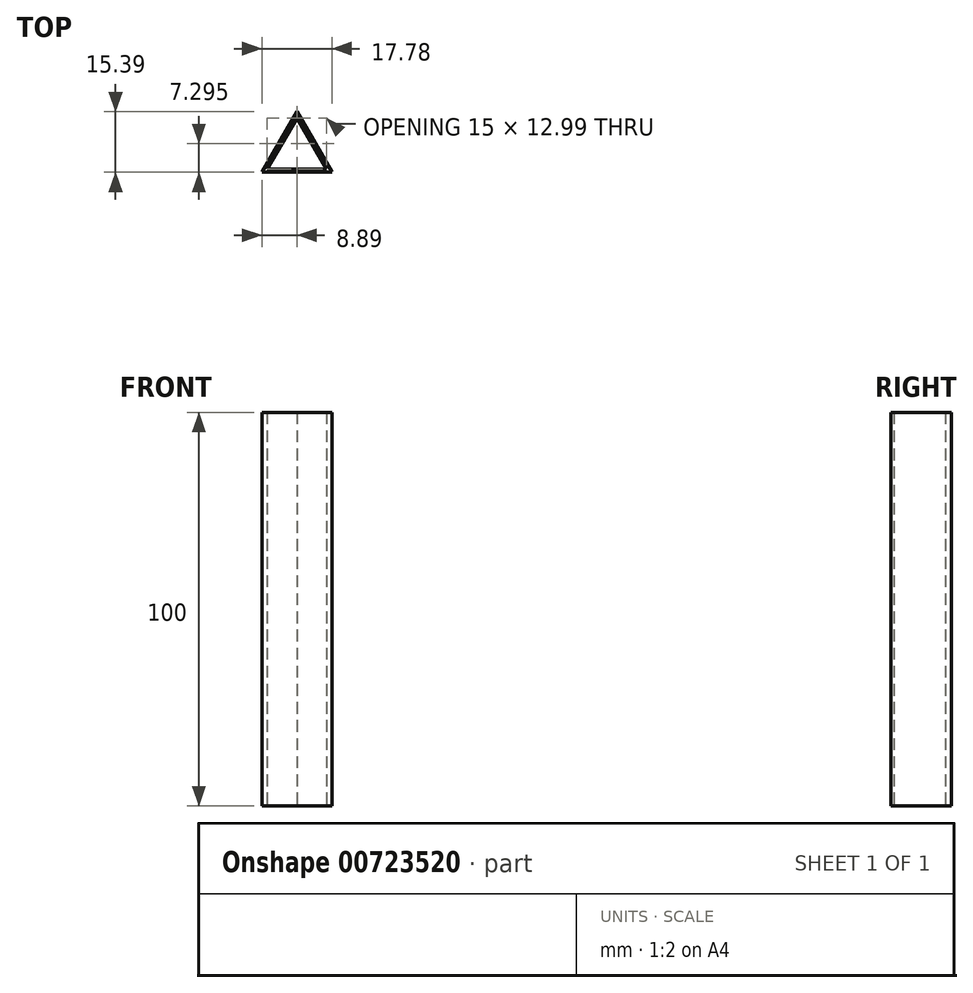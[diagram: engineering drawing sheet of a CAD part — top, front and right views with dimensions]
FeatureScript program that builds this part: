
annotation { "Feature Type Name" : "Feature", "Feature Type Description" : "" }
export const myFeature = defineFeature(function(context is Context, id is Id, definition is map)
    precondition{}
    {
        {
            var Q0;
            Q0=qCreatedBy(makeId("Top.planeOp"),FACE);
            var sketch = newSketch(context, id + "F0", { "sketchPlane" : qUnion([Q0])});
            skCircle(sketch, "E0.cCircle", {"center": v(0, 0) * mm, "radius": 8.66 * mm, "construction": true});
            skLineSegment(sketch, "E0.0", {"start": v(0, 8.66) * mm, "end": v(7.5, -4.33) * mm});
            skLineSegment(sketch, "E0.1", {"start": v(7.5, -4.33) * mm, "end": v(-7.5, -4.33) * mm});
            skLineSegment(sketch, "E0.2", {"start": v(-7.5, -4.33) * mm, "end": v(0, 8.66) * mm});
            skLineSegment(sketch, "E1.0", {"start": v(-8.89, -5.13) * mm, "end": v(0, 10.26) * mm});
            skLineSegment(sketch, "E1.1", {"start": v(8.89, -5.13) * mm, "end": v(-8.89, -5.13) * mm});
            skLineSegment(sketch, "E1.2", {"start": v(0, 10.26) * mm, "end": v(8.89, -5.13) * mm});
            skSolve(sketch);
        }
        {
            var Q0;
            Q0=makeQuery(id+"F0.imprint","IMPRINT",FACE,{"disambiguationData":[TD([[makeQuery(id+"F0.imprint","IMPRINT",EDGE,{"derivedFrom":sQuery(id+"F0.wireOp",EDGE,"E0.0")}),1.0]])]});
            extrude(context, id + "F1", {"entities" : qUnion([Q0]), "depth" : 100 * mm, "offsetDistance" : 25 * mm});
        }
    });
